annotation { "Feature Type Name" : "Feature", "Feature Type Description" : "" }
export const myFeature = defineFeature(function(context is Context, id is Id, definition is map)
    precondition{}
    {
        {
            var Q0;
            Q0=qCreatedBy(makeId("Front.planeOp"),FACE);
            var sketch = newSketch(context, id + "F0", { "sketchPlane" : qUnion([Q0])});
            skLineSegment(sketch, "E0.bottom", {"start": v(-96.59, 154.94) * mm, "end": v(119.31, 154.94) * mm});
            skLineSegment(sketch, "E0.top", {"start": v(-96.59, -60.96) * mm, "end": v(119.31, -60.96) * mm});
            skLineSegment(sketch, "E0.left", {"start": v(-96.59, 154.94) * mm, "end": v(-96.59, -60.96) * mm});
            skLineSegment(sketch, "E0.right", {"start": v(119.31, 154.94) * mm, "end": v(119.31, -60.96) * mm});
            skSolve(sketch);
        }
        {
            var Q0;
            Q0 = qSketchRegion(id + "F0", true);
            extrude(context, id + "F1", {"entities" : qUnion([Q0]), "depth" : 25.4 * mm, "offsetDistance" : 25.4 * mm});
        }
        {
            var Q0;
            Q0=makeQuery(id+"F1.opExtrude","CAP_FACE",FACE,{"disambiguationData":[OSD([sQuery(id+"F0.wireOp",EDGE,"E0.bottom"),sQuery(id+"F0.wireOp",EDGE,"E0.top"),sQuery(id+"F0.wireOp",EDGE,"E0.left"),sQuery(id+"F0.wireOp",EDGE,"E0.right")])],"isStart":false});
            var sketch = newSketch(context, id + "F2", { "sketchPlane" : qUnion([Q0])});
            skText(sketch, "E1", { "text": "Title Town", "fontName": "RobotoSlab-Regular.ttf"});
            skText(sketch, "E2", { "text": "1903  1912  1915  1916  1918\n1929  1939  1941  1957  1959\n1960  1960  1961  1962  1963\n1964  1965  1966  1968  1969\n1970  1972  1974  1976  1981\n1984  1986  2001  2003  2004\n2004  2007  2008  2011  2013\n2014  2016", "fontName": "Tinos-Regular.ttf"});
            const initialGuessF2  = {"E1": [-0.03944, 0.1343, 1, 0, 0.0143], "E2": [-0.09318, 0.08985, 1, 0, 0.0127]};
            skSetInitialGuess(sketch, initialGuessF2);
            skSolve(sketch);
        }
        {
            var Q0;
            Q0 = qSketchRegion(id + "F2", true);
            extrude(context, id + "F3", {"entities" : qUnion([Q0]), "operationType" : NewBodyOperationType.REMOVE, "oppositeDirection" : true, "depth" : 5.08 * mm, "offsetDistance" : 25.4 * mm});
        }
        {
            var Q0;
            {var subQ0=sQuery(id+"F0.wireOp",EDGE,"E0.right");var subQ1=sQuery(id+"F0.wireOp",EDGE,"E0.left");var subQ2=sQuery(id+"F0.wireOp",EDGE,"E0.top");var subQ3=sQuery(id+"F0.wireOp",EDGE,"E0.bottom");Q0=makeQuery(id+"F3.boolean.opBoolean","SPLIT",FACE,{"disambiguationData":[TD([makeQuery(id+"F1.opExtrude","SWEPT_FACE",FACE,{"disambiguationData":[OSD([subQ3])]})])],"derivedFrom":makeQuery(id+"F1.opExtrude","CAP_FACE",FACE,{"disambiguationData":[OSD([subQ3,subQ2,subQ1,subQ0])],"isStart":false})});}
            var sketch = newSketch(context, id + "F4", { "sketchPlane" : qUnion([Q0])});
            skLineSegment(sketch, "E3", {"start": v(88.83, 139.7) * mm, "end": v(119.31, 139.7) * mm, "construction": true});
            skCircle(sketch, "E4", {"center": v(104.07, 139.7) * mm, "radius": 14.99 * mm});
            skCircle(sketch, "E5", {"center": v(28.4, 117.1) * mm, "radius": 14.99 * mm});
            skArc(sketch, "E6", {"start": v(35.98, 126.97) * mm, "mid": v(33, 128.67) * mm, "end": v(29.66, 129.48) * mm});
            skLineSegment(sketch, "E7", {"start": v(-87.7, 152.3) * mm, "end": v(-88.65, 149.6) * mm});
            skArc(sketch, "E8", {"start": v(-88.97, 149.2) * mm, "mid": v(-88.68, 149.3) * mm, "end": v(-88.65, 149.6) * mm});
            skArc(sketch, "E9", {"start": v(-88.97, 149.2) * mm, "mid": v(-90.38, 147.19) * mm, "end": v(-91.03, 144.82) * mm});
            skArc(sketch, "E10", {"start": v(-93.81, 137.8) * mm, "mid": v(-92.24, 141.24) * mm, "end": v(-91.03, 144.82) * mm});
            skArc(sketch, "E11", {"start": v(-93.81, 137.8) * mm, "mid": v(-95.4, 135.76) * mm, "end": v(-95.85, 133.22) * mm});
            skArc(sketch, "E12", {"start": v(-95.85, 133.22) * mm, "mid": v(-94.25, 131.43) * mm, "end": v(-91.94, 130.75) * mm});
            skArc(sketch, "E13", {"start": v(-90.15, 130.13) * mm, "mid": v(-91.03, 130.5) * mm, "end": v(-91.94, 130.75) * mm});
            skLineSegment(sketch, "E14", {"start": v(-90.15, 130.13) * mm, "end": v(-82.9, 126.02) * mm});
            skArc(sketch, "E15", {"start": v(-82.9, 126.02) * mm, "mid": v(-81.73, 125.66) * mm, "end": v(-80.5, 125.82) * mm});
            skLineSegment(sketch, "E16", {"start": v(-80.5, 125.82) * mm, "end": v(-77.86, 126.27) * mm});
            skLineSegment(sketch, "E17", {"start": v(-77.86, 126.27) * mm, "end": v(-77.6, 127.73) * mm});
            skArc(sketch, "E18", {"start": v(-77.6, 127.73) * mm, "mid": v(-78.46, 129.44) * mm, "end": v(-79.66, 130.92) * mm});
            skLineSegment(sketch, "E19", {"start": v(-79.66, 130.92) * mm, "end": v(-78.9, 132.4) * mm});
            skArc(sketch, "E20", {"start": v(-74.1, 131.13) * mm, "mid": v(-76.48, 131.87) * mm, "end": v(-78.9, 132.4) * mm});
            skArc(sketch, "E21", {"start": v(-74.1, 131.13) * mm, "mid": v(-70.23, 130.87) * mm, "end": v(-66.65, 132.4) * mm});
            skArc(sketch, "E22", {"start": v(-66.65, 132.4) * mm, "mid": v(-67.7, 135.34) * mm, "end": v(-70.06, 137.35) * mm});
            skArc(sketch, "E23", {"start": v(-70.06, 137.35) * mm, "mid": v(-71.89, 137.83) * mm, "end": v(-73.77, 137.98) * mm});
            skArc(sketch, "E24", {"start": v(-77.88, 142.53) * mm, "mid": v(-76.67, 139.5) * mm, "end": v(-73.77, 137.98) * mm});
            skLineSegment(sketch, "E25", {"start": v(-77.88, 142.53) * mm, "end": v(-78.47, 148.91) * mm});
            skArc(sketch, "E26", {"start": v(-78.47, 148.91) * mm, "mid": v(-78.9, 149.99) * mm, "end": v(-79.84, 150.67) * mm});
            skLineSegment(sketch, "E27", {"start": v(-79.84, 150.67) * mm, "end": v(-80.23, 153.4) * mm});
            skArc(sketch, "E28", {"start": v(-80.23, 153.4) * mm, "mid": v(-80.47, 154.07) * mm, "end": v(-81.16, 154.3) * mm});
            skLineSegment(sketch, "E29", {"start": v(-81.16, 154.3) * mm, "end": v(-85.43, 153.98) * mm});
            skArc(sketch, "E30", {"start": v(-85.43, 153.98) * mm, "mid": v(-86.08, 153.63) * mm, "end": v(-86.28, 152.92) * mm});
            skArc(sketch, "E31", {"start": v(-86.28, 152.92) * mm, "mid": v(-87.12, 152.92) * mm, "end": v(-87.7, 152.3) * mm});
            skArc(sketch, "E32", {"start": v(-45.26, 119.12) * mm, "mid": v(-46.05, 118.21) * mm, "end": v(-45.02, 117.59) * mm});
            skArc(sketch, "E33", {"start": v(-45.02, 117.59) * mm, "mid": v(-41.26, 117.6) * mm, "end": v(-37.57, 118.34) * mm});
            skArc(sketch, "E34", {"start": v(-37.57, 118.34) * mm, "mid": v(-37.3, 117.58) * mm, "end": v(-36.53, 117.38) * mm});
            skArc(sketch, "E35", {"start": v(-36.53, 117.38) * mm, "mid": v(-32.82, 117.37) * mm, "end": v(-29.16, 117.97) * mm});
            skArc(sketch, "E36", {"start": v(-29.16, 117.97) * mm, "mid": v(-29.25, 117.01) * mm, "end": v(-28.4, 116.56) * mm});
            skArc(sketch, "E37", {"start": v(-12.9, 108.1) * mm, "mid": v(-19.84, 113.83) * mm, "end": v(-28.4, 116.56) * mm});
            skArc(sketch, "E38", {"start": v(-12.9, 108.1) * mm, "mid": v(-11.6, 109.02) * mm, "end": v(-10.82, 110.41) * mm});
            skLineSegment(sketch, "E39", {"start": v(-10.82, 110.41) * mm, "end": v(-10.82, 111.57) * mm});
            skLineSegment(sketch, "E40", {"start": v(-10.82, 111.57) * mm, "end": v(-10.93, 111.57) * mm});
            skLineSegment(sketch, "E41", {"start": v(-10.93, 111.57) * mm, "end": v(-10.9, 112.35) * mm});
            skLineSegment(sketch, "E42", {"start": v(-10.9, 112.35) * mm, "end": v(-10.77, 112.31) * mm});
            skLineSegment(sketch, "E43", {"start": v(-10.77, 112.31) * mm, "end": v(-10.77, 112.7) * mm});
            skLineSegment(sketch, "E44", {"start": v(-10.77, 112.7) * mm, "end": v(-9.69, 113.4) * mm});
            skLineSegment(sketch, "E45", {"start": v(-9.69, 113.4) * mm, "end": v(-10.37, 115.81) * mm});
            skLineSegment(sketch, "E46", {"start": v(-10.37, 115.81) * mm, "end": v(-8.59, 116.9) * mm});
            skLineSegment(sketch, "E47", {"start": v(-8.59, 116.9) * mm, "end": v(-6.93, 124.88) * mm});
            skArc(sketch, "E48", {"start": v(-6.93, 124.88) * mm, "mid": v(-6.84, 125.7) * mm, "end": v(-7.66, 125.58) * mm});
            skArc(sketch, "E49", {"start": v(-13.44, 125.9) * mm, "mid": v(-10.58, 125.28) * mm, "end": v(-7.66, 125.58) * mm});
            skArc(sketch, "E50", {"start": v(-13.44, 125.9) * mm, "mid": v(-22.66, 126.3) * mm, "end": v(-31.6, 124) * mm});
            skArc(sketch, "E51", {"start": v(-45.26, 119.12) * mm, "mid": v(-40.84, 120.51) * mm, "end": v(-36.5, 122.13) * mm});
            skArc(sketch, "E52", {"start": v(-36.5, 122.13) * mm, "mid": v(-34.03, 123.03) * mm, "end": v(-31.6, 124) * mm});
            skLineSegment(sketch, "E53", {"start": v(27.08, 129.48) * mm, "end": v(27.08, 124.7) * mm});
            skLineSegment(sketch, "E54", {"start": v(27.08, 124.7) * mm, "end": v(22.83, 124.7) * mm});
            skLineSegment(sketch, "E55", {"start": v(22.83, 124.7) * mm, "end": v(20.54, 126.74) * mm});
            skLineSegment(sketch, "E56", {"start": v(23.04, 120.88) * mm, "end": v(18.82, 125.04) * mm});
            skLineSegment(sketch, "E57", {"start": v(23.04, 120.88) * mm, "end": v(23.04, 118.61) * mm});
            skLineSegment(sketch, "E58", {"start": v(23.04, 118.61) * mm, "end": v(16.05, 118.61) * mm});
            skLineSegment(sketch, "E59", {"start": v(23.05, 116.09) * mm, "end": v(16, 116.09) * mm});
            skLineSegment(sketch, "E60", {"start": v(23.05, 116.09) * mm, "end": v(23.05, 113.98) * mm});
            skLineSegment(sketch, "E61", {"start": v(23.05, 113.98) * mm, "end": v(18.47, 109.6) * mm});
            skLineSegment(sketch, "E62", {"start": v(22.75, 110) * mm, "end": v(20.32, 107.63) * mm});
            skLineSegment(sketch, "E63", {"start": v(22.75, 110) * mm, "end": v(27, 110) * mm});
            skLineSegment(sketch, "E64", {"start": v(27, 110) * mm, "end": v(27, 104.73) * mm});
            skLineSegment(sketch, "E65", {"start": v(29.6, 109.84) * mm, "end": v(29.6, 104.71) * mm});
            skLineSegment(sketch, "E66", {"start": v(29.6, 109.84) * mm, "end": v(31.73, 109.84) * mm});
            skLineSegment(sketch, "E67", {"start": v(31.73, 109.84) * mm, "end": v(32.89, 111) * mm});
            skLineSegment(sketch, "E68", {"start": v(32.89, 111) * mm, "end": v(36.33, 107.5) * mm});
            skLineSegment(sketch, "E69", {"start": v(34.35, 113.18) * mm, "end": v(38.2, 109.43) * mm});
            skLineSegment(sketch, "E70", {"start": v(34.38, 116.23) * mm, "end": v(34.35, 113.18) * mm});
            skLineSegment(sketch, "E71", {"start": v(34.38, 116.23) * mm, "end": v(40.82, 116.23) * mm});
            skLineSegment(sketch, "E72", {"start": v(34.53, 118.78) * mm, "end": v(40.74, 118.78) * mm});
            skLineSegment(sketch, "E73", {"start": v(34.53, 118.78) * mm, "end": v(34.53, 121.7) * mm});
            skLineSegment(sketch, "E74", {"start": v(34.53, 121.7) * mm, "end": v(37.9, 125.14) * mm});
            skLineSegment(sketch, "E75", {"start": v(32.87, 124) * mm, "end": v(35.98, 126.97) * mm});
            skLineSegment(sketch, "E76", {"start": v(32.87, 124) * mm, "end": v(31.97, 124.94) * mm});
            skLineSegment(sketch, "E77", {"start": v(31.97, 124.94) * mm, "end": v(29.66, 124.92) * mm});
            skLineSegment(sketch, "E78", {"start": v(29.66, 124.92) * mm, "end": v(29.66, 129.48) * mm});
            skArc(sketch, "E79.trimOffspring", {"start": v(40.74, 118.78) * mm, "mid": v(39.77, 122.16) * mm, "end": v(37.9, 125.14) * mm});
            skArc(sketch, "E80.trimOffspring", {"start": v(38.2, 109.43) * mm, "mid": v(40.02, 112.63) * mm, "end": v(40.82, 116.23) * mm});
            skArc(sketch, "E81.trimOffspring", {"start": v(29.6, 104.71) * mm, "mid": v(33.17, 105.6) * mm, "end": v(36.33, 107.5) * mm});
            skArc(sketch, "E82.trimOffspring", {"start": v(16, 116.09) * mm, "mid": v(16.77, 112.67) * mm, "end": v(18.47, 109.6) * mm});
            skArc(sketch, "E83.trimOffspring", {"start": v(18.82, 125.04) * mm, "mid": v(16.97, 122.03) * mm, "end": v(16.05, 118.61) * mm});
            skArc(sketch, "E84.trimOffspring", {"start": v(27.08, 129.48) * mm, "mid": v(23.61, 128.59) * mm, "end": v(20.54, 126.74) * mm});
            skLineSegment(sketch, "E85", {"start": v(26.52, 121.32) * mm, "end": v(26.52, 118.9) * mm});
            skLineSegment(sketch, "E86", {"start": v(26.52, 118.9) * mm, "end": v(30, 118.9) * mm});
            skLineSegment(sketch, "E87", {"start": v(30, 118.9) * mm, "end": v(30.54, 119.4) * mm});
            skLineSegment(sketch, "E88", {"start": v(30.54, 119.4) * mm, "end": v(30.54, 120.79) * mm});
            skLineSegment(sketch, "E89", {"start": v(30.54, 120.79) * mm, "end": v(30, 121.32) * mm});
            skLineSegment(sketch, "E90", {"start": v(30, 121.32) * mm, "end": v(26.52, 121.32) * mm});
            skLineSegment(sketch, "E91", {"start": v(26.55, 115.93) * mm, "end": v(26.55, 113.5) * mm});
            skLineSegment(sketch, "E92", {"start": v(26.55, 113.5) * mm, "end": v(30.13, 113.44) * mm});
            skLineSegment(sketch, "E93", {"start": v(30.13, 113.44) * mm, "end": v(30.7, 113.91) * mm});
            skLineSegment(sketch, "E94", {"start": v(30.7, 113.91) * mm, "end": v(30.7, 115.49) * mm});
            skLineSegment(sketch, "E95", {"start": v(30.7, 115.49) * mm, "end": v(30.16, 115.93) * mm});
            skLineSegment(sketch, "E96", {"start": v(30.16, 115.93) * mm, "end": v(26.55, 115.93) * mm});
            skArc(sketch, "E97", {"start": v(99.73, 141.97) * mm, "mid": v(100.6, 139.98) * mm, "end": v(101.93, 138.27) * mm});
            skArc(sketch, "E98", {"start": v(100.92, 144.97) * mm, "mid": v(99.82, 143.67) * mm, "end": v(99.73, 141.97) * mm});
            skArc(sketch, "E99", {"start": v(103.73, 144.62) * mm, "mid": v(102.39, 145.28) * mm, "end": v(100.92, 144.97) * mm});
            skArc(sketch, "E100", {"start": v(101.93, 138.27) * mm, "mid": v(99.76, 138.87) * mm, "end": v(97.5, 138.85) * mm});
            skArc(sketch, "E101", {"start": v(97.5, 138.85) * mm, "mid": v(95.13, 136.97) * mm, "end": v(96.49, 134.27) * mm});
            skArc(sketch, "E102", {"start": v(96.49, 134.27) * mm, "mid": v(96.76, 131.87) * mm, "end": v(99.05, 131.08) * mm});
            skArc(sketch, "E103", {"start": v(99.05, 131.08) * mm, "mid": v(101.48, 132.28) * mm, "end": v(103.34, 134.24) * mm});
            skArc(sketch, "E104", {"start": v(103.34, 134.24) * mm, "mid": v(103.97, 130.58) * mm, "end": v(106.34, 127.73) * mm});
            skLineSegment(sketch, "E105", {"start": v(106.34, 127.73) * mm, "end": v(106.69, 128.86) * mm});
            skArc(sketch, "E106", {"start": v(104.63, 134.2) * mm, "mid": v(104.93, 131.25) * mm, "end": v(106.69, 128.86) * mm});
            skLineSegment(sketch, "E107", {"start": v(104.63, 134.2) * mm, "end": v(107.65, 131.38) * mm});
            skArc(sketch, "E108", {"start": v(107.65, 131.38) * mm, "mid": v(110.8, 131.17) * mm, "end": v(111.72, 134.2) * mm});
            skArc(sketch, "E109", {"start": v(111.72, 134.2) * mm, "mid": v(112.9, 136.8) * mm, "end": v(110.84, 138.78) * mm});
            skArc(sketch, "E110", {"start": v(110.84, 138.78) * mm, "mid": v(108.32, 138.86) * mm, "end": v(105.9, 138.15) * mm});
            skArc(sketch, "E111", {"start": v(105.9, 138.15) * mm, "mid": v(107.52, 140.76) * mm, "end": v(107.89, 143.8) * mm});
            skArc(sketch, "E112", {"start": v(107.89, 143.8) * mm, "mid": v(106.08, 145.55) * mm, "end": v(103.73, 144.62) * mm});
            skArc(sketch, "E113", {"start": v(20.32, 107.63) * mm, "mid": v(23.42, 105.64) * mm, "end": v(27, 104.73) * mm});
            skLineSegment(sketch, "E114", {"start": v(-81.88, 129.25) * mm, "end": v(-81.69, 126.8) * mm});
            skLineSegment(sketch, "E115", {"start": v(-81.69, 126.8) * mm, "end": v(-78.35, 126.88) * mm});
            skArc(sketch, "E116", {"start": v(-78.35, 126.88) * mm, "mid": v(-78.76, 128.37) * mm, "end": v(-79.62, 129.65) * mm});
            skLineSegment(sketch, "E117", {"start": v(-81.88, 129.25) * mm, "end": v(-79.62, 129.65) * mm});
            skArc(sketch, "E118", {"start": v(-93.97, 136.5) * mm, "mid": v(-94.93, 133.42) * mm, "end": v(-92.25, 131.63) * mm});
            skLineSegment(sketch, "E119", {"start": v(-93.97, 136.5) * mm, "end": v(-91.48, 135.23) * mm});
            skArc(sketch, "E120", {"start": v(-91.48, 135.23) * mm, "mid": v(-92.02, 133.46) * mm, "end": v(-92.25, 131.63) * mm});
            skLineSegment(sketch, "E121", {"start": v(-70.62, 131.9) * mm, "end": v(-71.5, 134.22) * mm});
            skLineSegment(sketch, "E122", {"start": v(-71.5, 134.22) * mm, "end": v(-69.25, 135.47) * mm});
            skArc(sketch, "E123", {"start": v(-67.42, 132.5) * mm, "mid": v(-67.97, 134.21) * mm, "end": v(-69.25, 135.47) * mm});
            skLineSegment(sketch, "E124", {"start": v(-70.62, 131.9) * mm, "end": v(-67.42, 132.5) * mm});
            skLineSegment(sketch, "E125", {"start": v(-85.07, 136.11) * mm, "end": v(-85.07, 137.14) * mm});
            skLineSegment(sketch, "E126", {"start": v(-85.07, 137.14) * mm, "end": v(-81.82, 136.31) * mm});
            skLineSegment(sketch, "E127", {"start": v(-81.82, 136.31) * mm, "end": v(-81.69, 133.33) * mm});
            skLineSegment(sketch, "E128", {"start": v(-81.69, 133.33) * mm, "end": v(-85.07, 136.11) * mm});
            skLineSegment(sketch, "E129", {"start": v(-14.41, 119.6) * mm, "end": v(-12.47, 120.33) * mm});
            skLineSegment(sketch, "E130", {"start": v(-12.47, 120.33) * mm, "end": v(-10.72, 118.73) * mm});
            skLineSegment(sketch, "E131", {"start": v(-10.72, 118.73) * mm, "end": v(-11.18, 120.76) * mm});
            skLineSegment(sketch, "E132", {"start": v(-11.18, 120.76) * mm, "end": v(-9.69, 121.3) * mm});
            skLineSegment(sketch, "E133", {"start": v(-9.69, 121.3) * mm, "end": v(-11.51, 121.87) * mm});
            skLineSegment(sketch, "E134", {"start": v(-11.51, 121.87) * mm, "end": v(-11.75, 123.16) * mm});
            skLineSegment(sketch, "E135", {"start": v(-11.75, 123.16) * mm, "end": v(-12.74, 122.14) * mm});
            skLineSegment(sketch, "E136", {"start": v(-12.74, 122.14) * mm, "end": v(-14.56, 122.55) * mm});
            skLineSegment(sketch, "E137", {"start": v(-14.56, 122.55) * mm, "end": v(-13.44, 121.2) * mm});
            skLineSegment(sketch, "E138", {"start": v(-13.44, 121.2) * mm, "end": v(-14.41, 119.6) * mm});
            skSolve(sketch);
        }
        {
            var Q0;
            Q0 = qSketchRegion(id + "F4", true);
            extrude(context, id + "F5", {"entities" : qUnion([Q0]), "operationType" : NewBodyOperationType.REMOVE, "oppositeDirection" : true, "depth" : 2.54 * mm, "offsetDistance" : 25.4 * mm});
        }
    });